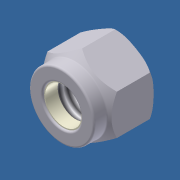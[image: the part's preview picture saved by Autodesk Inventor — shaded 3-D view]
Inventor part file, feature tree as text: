
AUTODESK INVENTOR PART (.ipt)
format: ipt  version: 2012 (Build 160160000, 160)  size: 153,600 bytes
history: native  units: in
note: dims shown in document units (in); Inventor stores cm internally (conversion verified against a paired STEP export)
features: revolve x3, sketch x2, extrude x1, hole x1, fillet x1, projected_geometry x1
ambient origin geometry x8: Origin, YZ Plane, XZ Plane, XY Plane, X Axis, Y Axis, Z Axis, Center Point
bodies: Solid1 (feature_tree)
feature tree (9):
  extrude  "Extrusion1"  Depth=0.458in TaperAngle=0.0deg
  sketch  "Sketch2"  dims[d3=0.165in d4=45.0deg d5=0.2595in d6=0.145in d7=0.015in d8=0.1in d9=0.1in d10=90.0deg d11=0.2775in d12=0.03in d13=0.1in d14=90.0deg d15=1.0in d16=1.0in d17=0.307in d18=0.5in d19=0.375in d20=0.25in d21=0.5635in d22=0.75in d23=0.8108in d24=0.015in d25=90.0deg]
  revolve  "Revolution1"  Angle=45.0deg
  revolve  "Revolution2"  [1 undecoded]
  hole  "Hole1"  [1 undecoded]
  fillet  "Fillet1"  Radius=0.015in
  revolve  "Revolution3"  [1 undecoded]
  sketch  "Sketch1"  dims[d0=0.555in d1=0.458in d2=0.0in]
  projected_geometry  "Projected Loop1"
note: 3 required parameter values undecoded (feature->parameter linkage not recoverable at this tier; creation-order binding heuristic only, values carry confidence <= 0.55)